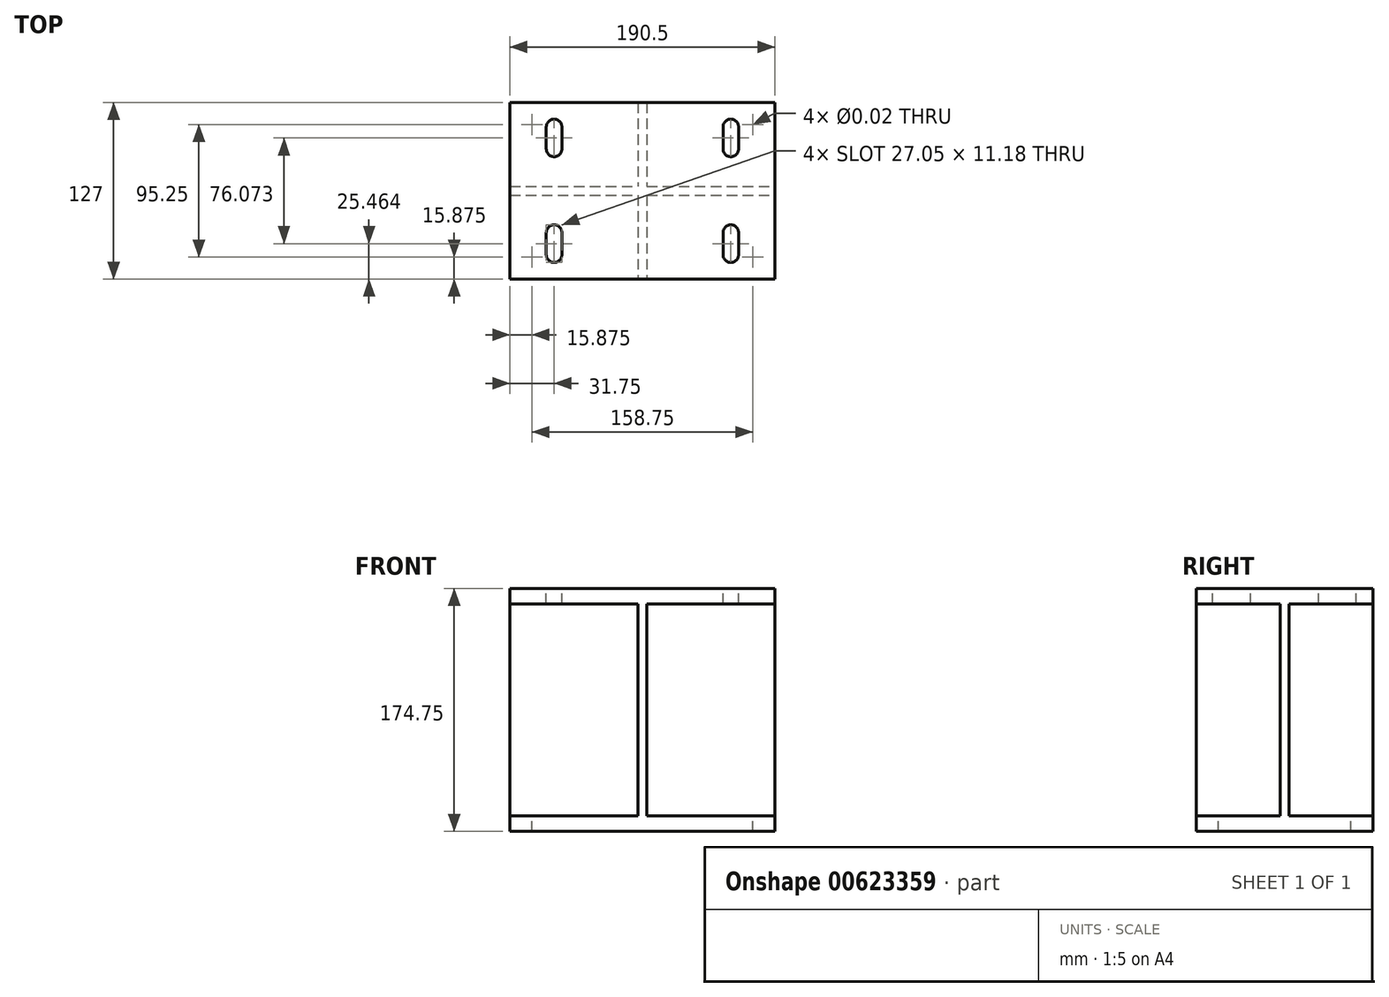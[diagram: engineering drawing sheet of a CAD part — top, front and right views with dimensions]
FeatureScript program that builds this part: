
annotation { "Feature Type Name" : "Feature", "Feature Type Description" : "" }
export const myFeature = defineFeature(function(context is Context, id is Id, definition is map)
    precondition{}
    {
        {
            var Q0;
            Q0=qCreatedBy(makeId("Top.planeOp"),FACE);
            var sketch = newSketch(context, id + "F0", { "sketchPlane" : qUnion([Q0])});
            skLineSegment(sketch, "E0.bottom", {"start": v(-95.25, 63.5) * mm, "end": v(95.25, 63.5) * mm});
            skLineSegment(sketch, "E0.top", {"start": v(-95.25, -63.5) * mm, "end": v(95.25, -63.5) * mm});
            skLineSegment(sketch, "E0.left", {"start": v(-95.25, 63.5) * mm, "end": v(-95.25, -63.5) * mm});
            skLineSegment(sketch, "E0.right", {"start": v(95.25, 63.5) * mm, "end": v(95.25, -63.5) * mm});
            skPoint(sketch, "E0.middle", {"position": v(0, 0) * mm});
            skSolve(sketch);
        }
        {
            var Q0;
            Q0 = qSketchRegion(id + "F0", true);
            extrude(context, id + "F1", {"entities" : qUnion([Q0]), "depth" : 11.18 * mm, "offsetDistance" : 25.4 * mm});
        }
        {
            var Q0;
            Q0=makeQuery(id+"F1.opExtrude","CAP_FACE",FACE,{"disambiguationData":[OSD([sQuery(id+"F0.wireOp",EDGE,"E0.bottom"),sQuery(id+"F0.wireOp",EDGE,"E0.top"),sQuery(id+"F0.wireOp",EDGE,"E0.left"),sQuery(id+"F0.wireOp",EDGE,"E0.right")])],"isStart":false});
            var sketch = newSketch(context, id + "F2", { "sketchPlane" : qUnion([Q0])});
            skLineSegment(sketch, "E1.bottom", {"start": v(-79.37, 47.63) * mm, "end": v(79.38, 47.63) * mm, "construction": true});
            skLineSegment(sketch, "E1.top", {"start": v(-79.38, -47.63) * mm, "end": v(79.37, -47.63) * mm, "construction": true});
            skLineSegment(sketch, "E1.left", {"start": v(-79.37, 47.63) * mm, "end": v(-79.38, -47.63) * mm, "construction": true});
            skLineSegment(sketch, "E1.right", {"start": v(79.38, 47.63) * mm, "end": v(79.37, -47.63) * mm, "construction": true});
            skPoint(sketch, "E1.middle", {"position": v(0, 0) * mm});
            skPoint(sketch, "E2", {"position": v(-79.37, 47.63) * mm});
            skPoint(sketch, "E3", {"position": v(79.38, 47.63) * mm});
            skPoint(sketch, "E4", {"position": v(-79.38, -47.63) * mm});
            skPoint(sketch, "E5", {"position": v(79.37, -47.63) * mm});
            skSolve(sketch);
        }
        {
            var Q0;
            Q0=sQuery(id+"F2.wireOp",VERTEX,"E2");
            var Q1;
            Q1=sQuery(id+"F2.wireOp",VERTEX,"E3");
            var Q2;
            Q2=sQuery(id+"F2.wireOp",VERTEX,"E4");
            var Q3;
            Q3=sQuery(id+"F2.wireOp",VERTEX,"E5");
            var Q4;
            Q4=makeQuery(id+"F1.opExtrude","SWEPT_BODY",BODY,{"disambiguationData":[OSD([sQuery(id+"F0.wireOp",EDGE,"E0.bottom"),sQuery(id+"F0.wireOp",EDGE,"E0.top"),sQuery(id+"F0.wireOp",EDGE,"E0.left"),sQuery(id+"F0.wireOp",EDGE,"E0.right")])]});
            hole(context, id + "F3", {"style" : HoleStyle.SIMPLE, "endStyle" : HoleEndStyle.THROUGH, "standardTappedOrClearance" : lookupTablePath({ "standard" : "ANSI", "size" : "9/16 (0.56)", "type" : "Drilled" }), "standardBlindInLast" : lookupTablePath({ "standard" : "ANSI", "size" : "9/16", "type" : "Drilled" }), "holeDiameter" : 9 / 406.4 * mm, "majorDiameter" : 6.35 * mm, "isTappedThrough" : true, "tappedDepth" : 15.24 * mm, "tapClearance" : 3, "locations" : qUnion([Q0, Q1, Q2, Q3]), "scope" : qUnion([Q4])});
        }
        {
            var Q0;
            Q0=makeQuery(id+"F1.opExtrude","CAP_FACE",FACE,{"disambiguationData":[OSD([sQuery(id+"F0.wireOp",EDGE,"E0.bottom"),sQuery(id+"F0.wireOp",EDGE,"E0.top"),sQuery(id+"F0.wireOp",EDGE,"E0.left"),sQuery(id+"F0.wireOp",EDGE,"E0.right")])],"isStart":false});
            var sketch = newSketch(context, id + "F4", { "sketchPlane" : qUnion([Q0])});
            skLineSegment(sketch, "E6", {"start": v(0, 90.21) * mm, "end": v(0, -105.62) * mm, "construction": true});
            skLineSegment(sketch, "E7", {"start": v(-144.3, 0) * mm, "end": v(133.01, 0) * mm, "construction": true});
            skLineSegment(sketch, "E8.bottom", {"start": v(-95.25, 3.17) * mm, "end": v(95.25, 3.17) * mm});
            skLineSegment(sketch, "E8.top", {"start": v(-95.25, -3.18) * mm, "end": v(95.25, -3.18) * mm});
            skLineSegment(sketch, "E8.left", {"start": v(-95.25, 3.17) * mm, "end": v(-95.25, -3.18) * mm});
            skLineSegment(sketch, "E8.right", {"start": v(95.25, 3.17) * mm, "end": v(95.25, -3.18) * mm});
            skPoint(sketch, "E8.middle", {"position": v(0, 0) * mm});
            skLineSegment(sketch, "E9.bottom", {"start": v(-3.17, 63.5) * mm, "end": v(3.18, 63.5) * mm});
            skLineSegment(sketch, "E9.top", {"start": v(-3.18, -63.5) * mm, "end": v(3.17, -63.5) * mm});
            skLineSegment(sketch, "E9.left", {"start": v(-3.17, 63.5) * mm, "end": v(-3.18, -63.5) * mm});
            skLineSegment(sketch, "E9.right", {"start": v(3.18, 63.5) * mm, "end": v(3.17, -63.5) * mm});
            skSolve(sketch);
        }
        {
            var Q0;
            Q0 = qSketchRegion(id + "F4", true);
            extrude(context, id + "F5", {"entities" : qUnion([Q0]), "operationType" : NewBodyOperationType.ADD, "depth" : 152.4 * mm, "offsetDistance" : 25.4 * mm});
        }
        {
            var Q0;
            Q0=makeQuery(id+"F5.opExtrude","CAP_FACE",FACE,{"disambiguationData":[OSD([sQuery(id+"F4.wireOp",EDGE,"E8.bottom"),sQuery(id+"F4.wireOp",EDGE,"E8.top"),sQuery(id+"F4.wireOp",EDGE,"E8.left"),sQuery(id+"F4.wireOp",EDGE,"E8.right"),sQuery(id+"F4.wireOp",EDGE,"E9.bottom"),sQuery(id+"F4.wireOp",EDGE,"E9.top"),sQuery(id+"F4.wireOp",EDGE,"E9.left"),sQuery(id+"F4.wireOp",EDGE,"E9.right")])],"isStart":false});
            var sketch = newSketch(context, id + "F6", { "sketchPlane" : qUnion([Q0])});
            skLineSegment(sketch, "E10.0", {"start": v(-95.25, 63.5) * mm, "end": v(-3.17, 63.5) * mm, "construction": true});
            skLineSegment(sketch, "E11.0", {"start": v(3.17, -63.5) * mm, "end": v(95.25, -63.5) * mm, "construction": true});
            skLineSegment(sketch, "E12.bottom", {"start": v(-95.25, 63.5) * mm, "end": v(95.25, 63.5) * mm});
            skLineSegment(sketch, "E12.top", {"start": v(-95.25, -63.5) * mm, "end": v(95.25, -63.5) * mm});
            skLineSegment(sketch, "E12.left", {"start": v(-95.25, 63.5) * mm, "end": v(-95.25, -63.5) * mm});
            skLineSegment(sketch, "E12.right", {"start": v(95.25, 63.5) * mm, "end": v(95.25, -63.5) * mm});
            skSolve(sketch);
        }
        {
            var Q0;
            Q0 = qSketchRegion(id + "F6", true);
            extrude(context, id + "F7", {"entities" : qUnion([Q0]), "operationType" : NewBodyOperationType.ADD, "depth" : 11.18 * mm, "offsetDistance" : 25.4 * mm});
        }
        {
            var Q0;
            Q0=makeQuery(id+"F7.opExtrude","CAP_FACE",FACE,{"disambiguationData":[OSD([sQuery(id+"F6.wireOp",EDGE,"E12.bottom"),sQuery(id+"F6.wireOp",EDGE,"E12.top"),sQuery(id+"F6.wireOp",EDGE,"E12.left"),sQuery(id+"F6.wireOp",EDGE,"E12.right")])],"isStart":false});
            var sketch = newSketch(context, id + "F8", { "sketchPlane" : qUnion([Q0])});
            skLineSegment(sketch, "E13", {"start": v(0, 87.95) * mm, "end": v(0, -88.24) * mm, "construction": true});
            skLineSegment(sketch, "E14.0", {"start": v(-63.5, 87.95) * mm, "end": v(-63.5, 0) * mm, "construction": true});
            skLineSegment(sketch, "E15", {"start": v(-124.8, 0) * mm, "end": v(140.35, 0) * mm, "construction": true});
            skLineSegment(sketch, "E16.0", {"start": v(-63.5, -38.1) * mm, "end": v(140.35, -38.1) * mm, "construction": true});
            skLineSegment(sketch, "E17", {"start": v(-63.5, -38.1) * mm, "end": v(-63.5, -45.97) * mm});
            skLineSegment(sketch, "E18", {"start": v(-63.5, -45.97) * mm, "end": v(-63.5, -30.1) * mm});
            skArc(sketch, "E19.0.startCap", {"start": v(-57.91, -45.97) * mm, "mid": v(-63.5, -51.56) * mm, "end": v(-69.09, -45.97) * mm});
            skArc(sketch, "E19.0.endCap", {"start": v(-69.09, -30.1) * mm, "mid": v(-63.5, -24.51) * mm, "end": v(-57.91, -30.1) * mm});
            skLineSegment(sketch, "E19.0.left", {"start": v(-69.09, -45.97) * mm, "end": v(-69.09, -30.1) * mm});
            skLineSegment(sketch, "E19.0.right", {"start": v(-57.91, -45.97) * mm, "end": v(-57.91, -30.1) * mm});
            skLineSegment(sketch, "E20.MirrorCS", {"start": v(-63.5, 38.1) * mm, "end": v(-63.5, 45.97) * mm});
            skLineSegment(sketch, "E21.MirrorCS", {"start": v(-57.91, 45.97) * mm, "end": v(-57.91, 30.1) * mm});
            skLineSegment(sketch, "E22.MirrorCS", {"start": v(-69.09, 45.97) * mm, "end": v(-69.09, 30.1) * mm});
            skArc(sketch, "E23.MirrorCS", {"start": v(-69.09, 30.1) * mm, "mid": v(-63.5, 24.51) * mm, "end": v(-57.91, 30.1) * mm});
            skArc(sketch, "E24.MirrorCS", {"start": v(-57.91, 45.97) * mm, "mid": v(-63.5, 51.56) * mm, "end": v(-69.09, 45.97) * mm});
            skLineSegment(sketch, "E25.MirrorCS", {"start": v(-63.5, 45.97) * mm, "end": v(-63.5, 30.1) * mm});
            skLineSegment(sketch, "E26.MirrorCS", {"start": v(63.5, -38.1) * mm, "end": v(63.5, -45.97) * mm});
            skLineSegment(sketch, "E27.MirrorCS", {"start": v(69.09, 45.97) * mm, "end": v(69.09, 30.1) * mm});
            skLineSegment(sketch, "E28.MirrorCS", {"start": v(57.91, 45.97) * mm, "end": v(57.91, 30.1) * mm});
            skLineSegment(sketch, "E29.MirrorCS", {"start": v(63.5, 38.1) * mm, "end": v(63.5, 45.97) * mm});
            skLineSegment(sketch, "E30.MirrorCS", {"start": v(57.91, -45.97) * mm, "end": v(57.91, -30.1) * mm});
            skLineSegment(sketch, "E31.MirrorCS", {"start": v(69.09, -45.97) * mm, "end": v(69.09, -30.1) * mm});
            skArc(sketch, "E32.MirrorCS", {"start": v(69.09, 30.1) * mm, "mid": v(63.5, 24.51) * mm, "end": v(57.91, 30.1) * mm});
            skArc(sketch, "E33.MirrorCS", {"start": v(57.91, 45.97) * mm, "mid": v(63.5, 51.56) * mm, "end": v(69.09, 45.97) * mm});
            skLineSegment(sketch, "E34.MirrorCS", {"start": v(63.5, 45.97) * mm, "end": v(63.5, 30.1) * mm});
            skLineSegment(sketch, "E35.MirrorCS", {"start": v(63.5, -45.97) * mm, "end": v(63.5, -30.1) * mm});
            skArc(sketch, "E36.MirrorCS", {"start": v(57.91, -45.97) * mm, "mid": v(63.5, -51.56) * mm, "end": v(69.09, -45.97) * mm});
            skArc(sketch, "E37.MirrorCS", {"start": v(69.09, -30.1) * mm, "mid": v(63.5, -24.51) * mm, "end": v(57.91, -30.1) * mm});
            skSolve(sketch);
        }
        {
            var Q0;
            Q0 = qSketchRegion(id + "F8", true);
            extrude(context, id + "F9", {"entities" : qUnion([Q0]), "operationType" : NewBodyOperationType.REMOVE, "oppositeDirection" : true, "depth" : 25.4 * mm, "offsetDistance" : 25.4 * mm});
        }
    });
